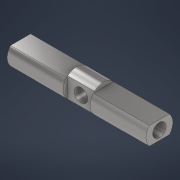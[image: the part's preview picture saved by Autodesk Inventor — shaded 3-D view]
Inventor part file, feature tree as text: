
AUTODESK INVENTOR PART (.ipt)
format: ipt  version: 2025 (Build 290162010, 162A)  size: 154,624 bytes
history: native  units: mm
features: extrude x5, move_body x2, direct_edit x1, sketch x1, projected_geometry x1
ambient origin geometry x8: Origin, YZ Plane, XZ Plane, XY Plane, X Axis, Y Axis, Z Axis, Center Point
bodies: Solid1 (feature_tree)
feature tree (10):
  extrude  "Extrusion1"  Depth=4.0mm TaperAngle=0.0deg
  extrude  "Extrusion2"  Depth=4.0mm
  extrude  "Extrusion3"  Depth=7.0mm
  extrude  "Extrusion4"  Depth=4.0mm
  extrude  "Extrusion5"  Depth=4.0mm TaperAngle=0.0deg
  direct_edit  "Direct Edit1"
  sketch  "Sketch2"  dims[d0=6.0mm d1=31.0mm d2=0.0mm d3=1.0mm d4=7.0mm d5=1.0mm d6=6.0mm d7=0.0mm d8=3.0mm d9=0.0mm d10=0.0mm d11=3.0mm d12=6.0mm d13=6.0mm d14=4.0mm d15=5.5mm d16=0.0mm d17=6.0mm d18=5.5mm d19=0.0mm d20=0.0mm d21=0.0mm d22=-7.0mm d23=0.0mm d24=0.0mm d25=-7.0mm]
  projected_geometry  "Projected Loop1"
  move_body  "Move1"
  move_body  "Move2"
